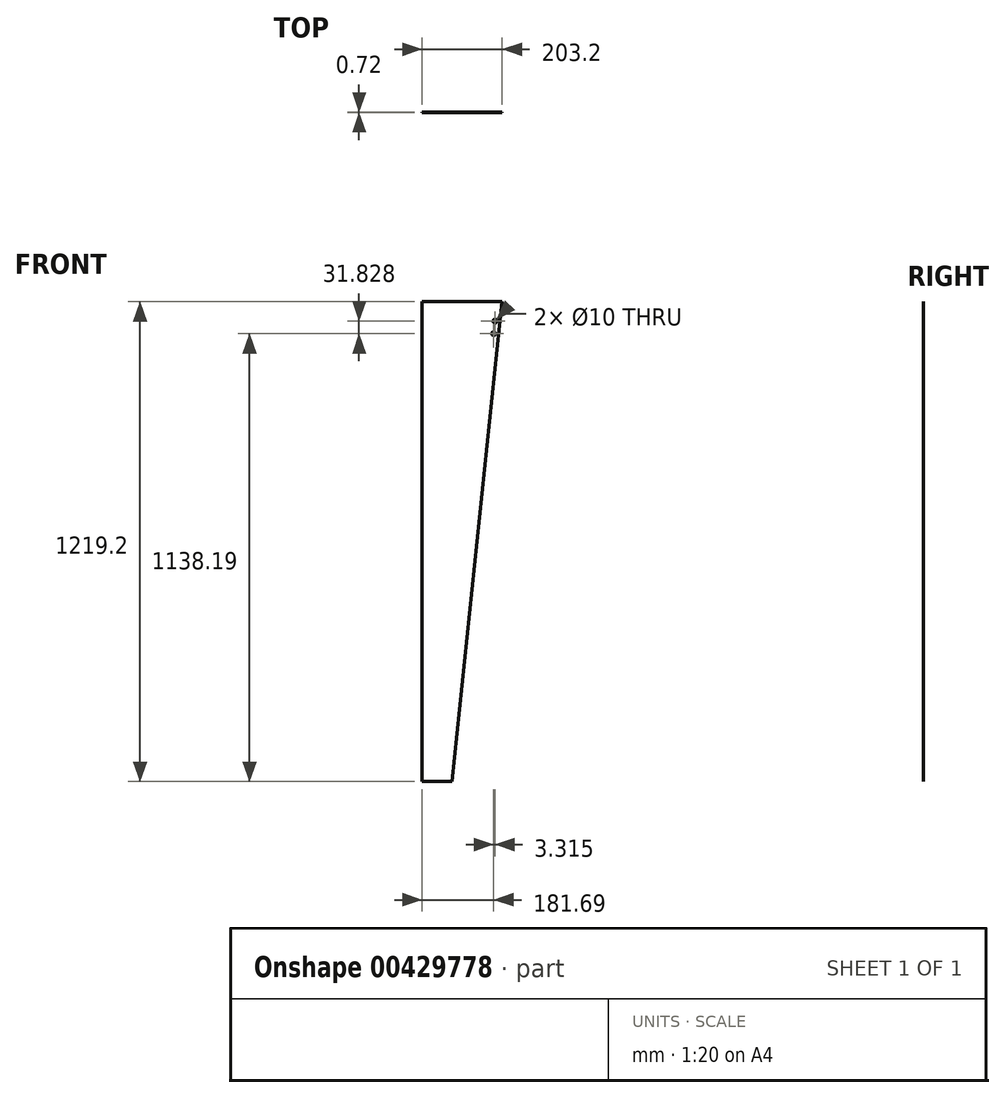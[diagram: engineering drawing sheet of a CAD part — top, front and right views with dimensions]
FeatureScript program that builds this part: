
annotation { "Feature Type Name" : "Feature", "Feature Type Description" : "" }
export const myFeature = defineFeature(function(context is Context, id is Id, definition is map)
    precondition{}
    {
        {
            var Q0;
            Q0=qCreatedBy(makeId("Front.planeOp"),FACE);
            var sketch = newSketch(context, id + "F0", { "sketchPlane" : qUnion([Q0])});
            skLineSegment(sketch, "E0", {"start": v(-304.61, -87.3) * mm, "end": v(-304.61, 1131.9) * mm});
            skLineSegment(sketch, "E1", {"start": v(-304.61, 1131.9) * mm, "end": v(-101.41, 1131.9) * mm});
            skLineSegment(sketch, "E2", {"start": v(-101.41, 1131.9) * mm, "end": v(-228.41, -87.3) * mm});
            skLineSegment(sketch, "E3", {"start": v(-228.41, -87.3) * mm, "end": v(-304.61, -87.3) * mm});
            skSolve(sketch);
        }
        {
            assignVariable(context, id + "F1", {"name" : "thick", "anyValue" : .72});
        }
        {
            var Q0;
            Q0 = qSketchRegion(id + "F0", true);
            extrude(context, id + "F2", {"entities" : qUnion([Q0]), "depth" : (getVariable(context, 'thick')) * mm});
        }
        {
            var Q0;
            Q0=makeQuery(id+"F2.opExtrude","CAP_FACE",FACE,{"disambiguationData":[OSD([sQuery(id+"F0.wireOp",EDGE,"E0"),sQuery(id+"F0.wireOp",EDGE,"E1"),sQuery(id+"F0.wireOp",EDGE,"E2"),sQuery(id+"F0.wireOp",EDGE,"E3")])],"isStart":false});
            var sketch = newSketch(context, id + "F3", { "sketchPlane" : qUnion([Q0])});
            skPoint(sketch, "E4", {"position": v(-119.6, 1082.72) * mm});
            skPoint(sketch, "E5", {"position": v(-122.92, 1050.9) * mm});
            skLineSegment(sketch, "E6", {"start": v(-101.41, 1131.9) * mm, "end": v(-78.95, 1129.56) * mm, "construction": true});
            skSolve(sketch);
        }
        {
            var Q0;
            Q0=sQuery(id+"F3.wireOp",VERTEX,"E4");
            var Q1;
            Q1=sQuery(id+"F3.wireOp",VERTEX,"E5");
            var Q2;
            Q2=makeQuery(id+"F2.opExtrude","SWEPT_BODY",BODY,{"disambiguationData":[OSD([sQuery(id+"F0.wireOp",EDGE,"E0"),sQuery(id+"F0.wireOp",EDGE,"E1"),sQuery(id+"F0.wireOp",EDGE,"E2"),sQuery(id+"F0.wireOp",EDGE,"E3")])]});
            hole(context, id + "F4", {"style" : HoleStyle.SIMPLE, "endStyle" : HoleEndStyle.BLIND, "holeDiameter" : 10 * mm, "holeDepth" : 11.5 * mm, "isTappedThrough" : true, "tappedDepth" : 12.7 * mm, "tapClearance" : 3, "locations" : qUnion([Q0, Q1]), "scope" : qUnion([Q2])});
        }
    });
